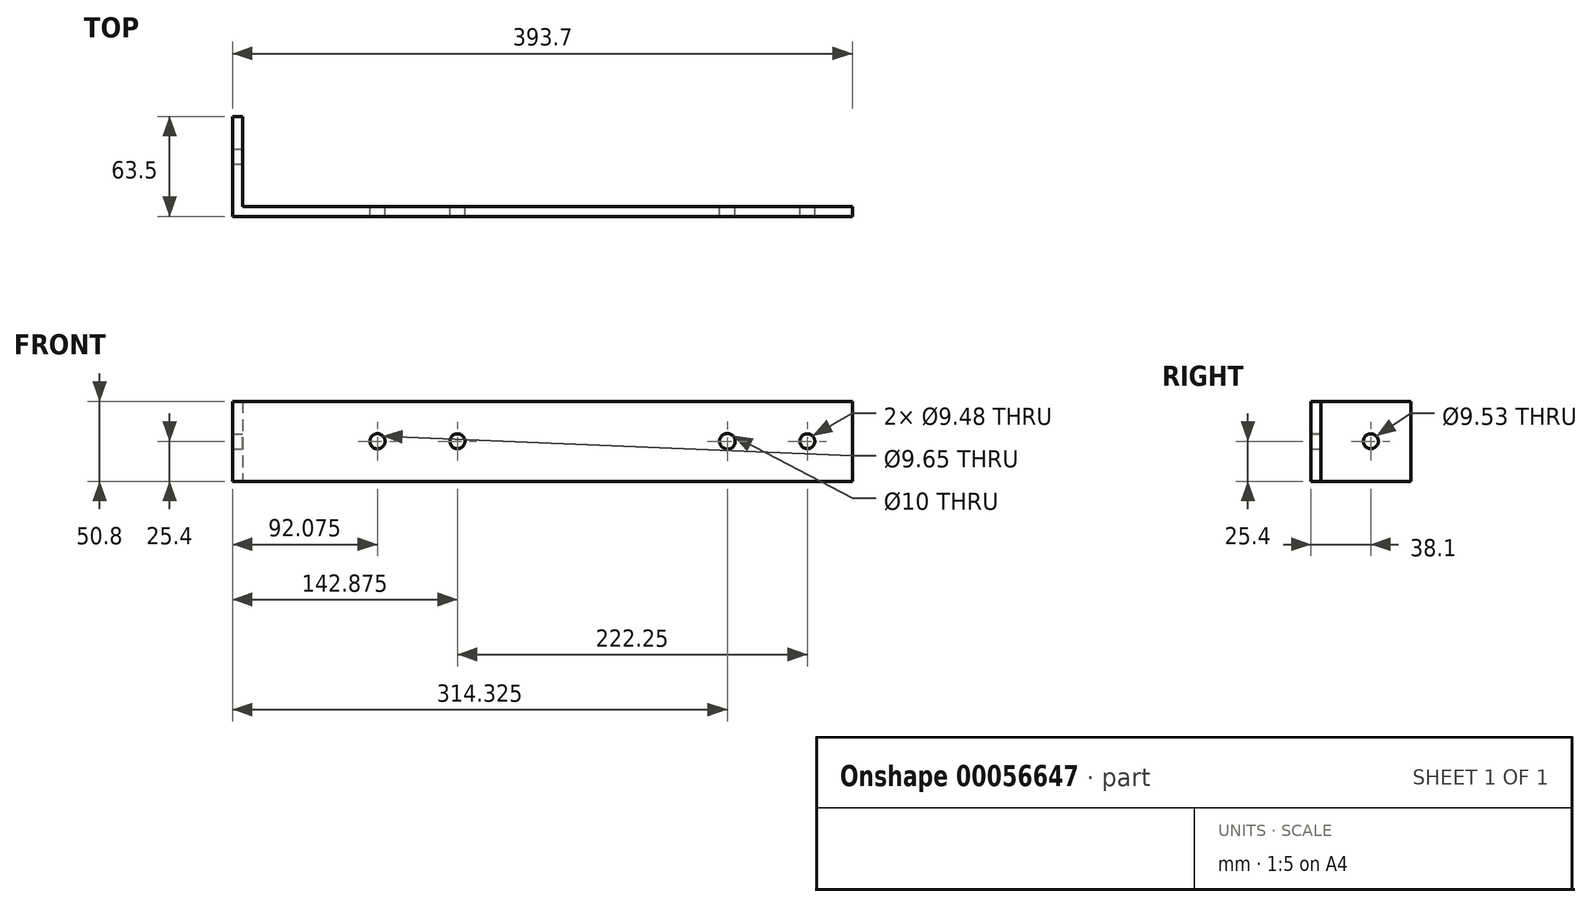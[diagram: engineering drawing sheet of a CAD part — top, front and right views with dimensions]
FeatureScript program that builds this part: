
annotation { "Feature Type Name" : "Feature", "Feature Type Description" : "" }
export const myFeature = defineFeature(function(context is Context, id is Id, definition is map)
    precondition{}
    {
        {
            var Q0;
            Q0=qCreatedBy(makeId("Top.planeOp"),FACE);
            var sketch = newSketch(context, id + "F0", { "sketchPlane" : qUnion([Q0])});
            skLineSegment(sketch, "E0", {"start": v(393.7, 0) * mm, "end": v(0, 0) * mm});
            skLineSegment(sketch, "E1", {"start": v(0, 0) * mm, "end": v(0, 63.5) * mm});
            skLineSegment(sketch, "E2", {"start": v(6.35, 63.5) * mm, "end": v(6.35, 6.35) * mm});
            skLineSegment(sketch, "E3", {"start": v(6.35, 6.35) * mm, "end": v(393.7, 6.35) * mm});
            skLineSegment(sketch, "E4", {"start": v(393.7, 6.35) * mm, "end": v(393.7, 0) * mm});
            skLineSegment(sketch, "E5", {"start": v(6.35, 63.5) * mm, "end": v(0, 63.5) * mm});
            skSolve(sketch);
        }
        {
            var Q0;
            Q0 = qSketchRegion(id + "F0", true);
            extrude(context, id + "F1", {"entities" : qUnion([Q0]), "endBound" : BoundingType.SYMMETRIC, "depth" : 50.8 * mm});
        }
        {
            var Q0;
            Q0=makeQuery(id+"F1.opExtrude","SWEPT_FACE",FACE,{"disambiguationData":[OSD([sQuery(id+"F0.wireOp",EDGE,"E2")])]});
            var sketch = newSketch(context, id + "F2", { "sketchPlane" : qUnion([Q0])});
            skCircle(sketch, "E6", {"center": v(38.1, 0) * mm, "radius": 4.76 * mm});
            skSolve(sketch);
        }
        {
            var Q0;
            Q0 = qSketchRegion(id + "F2", true);
            extrude(context, id + "F3", {"entities" : qUnion([Q0]), "operationType" : NewBodyOperationType.REMOVE, "endBound" : BoundingType.THROUGH_ALL, "oppositeDirection" : true, "depth" : 25.4 * mm});
        }
        {
            var Q0;
            Q0=makeQuery(id+"F1.opExtrude","SWEPT_FACE",FACE,{"disambiguationData":[OSD([sQuery(id+"F0.wireOp",EDGE,"E3")])]});
            var sketch = newSketch(context, id + "F4", { "sketchPlane" : qUnion([Q0])});
            skCircle(sketch, "E7", {"center": v(-365.13, 0) * mm, "radius": 4.74 * mm});
            skCircle(sketch, "E8", {"center": v(-314.33, 0) * mm, "radius": 5 * mm});
            skCircle(sketch, "E9", {"center": v(-142.88, 0) * mm, "radius": 4.74 * mm});
            skCircle(sketch, "E10", {"center": v(-92.08, 0) * mm, "radius": 4.83 * mm});
            skSolve(sketch);
        }
        {
            var Q0;
            Q0 = qSketchRegion(id + "F4", true);
            extrude(context, id + "F5", {"entities" : qUnion([Q0]), "operationType" : NewBodyOperationType.REMOVE, "endBound" : BoundingType.THROUGH_ALL, "oppositeDirection" : true, "depth" : 25.4 * mm});
        }
    });
